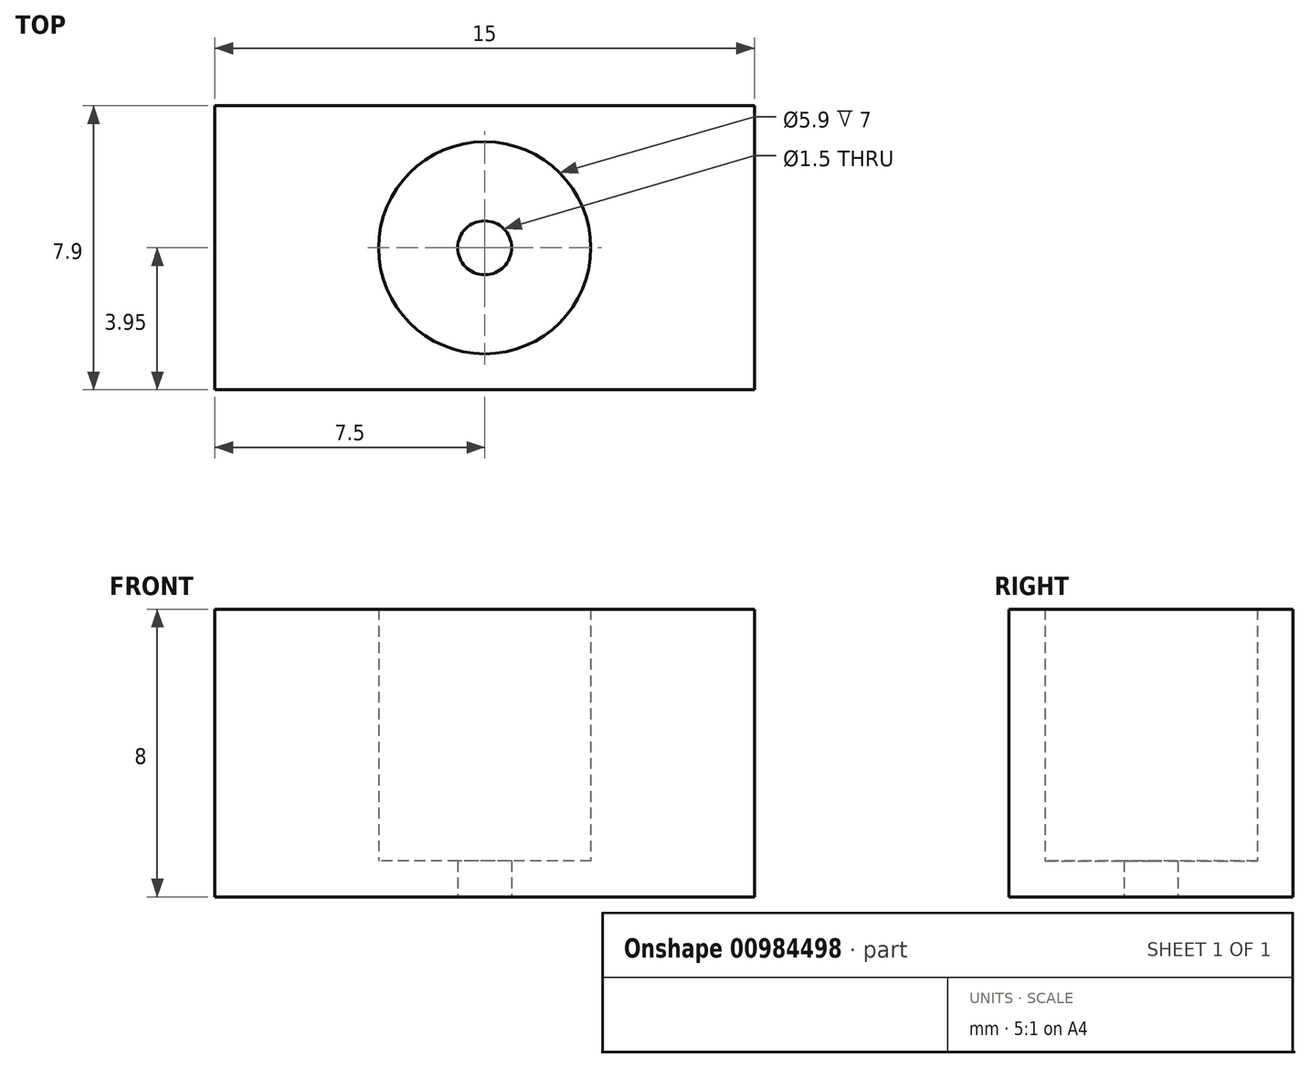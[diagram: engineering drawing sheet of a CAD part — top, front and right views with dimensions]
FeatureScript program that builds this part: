
annotation { "Feature Type Name" : "Feature", "Feature Type Description" : "" }
export const myFeature = defineFeature(function(context is Context, id is Id, definition is map)
    precondition{}
    {
        {
            var Q0;
            Q0=qCreatedBy(makeId("Top.planeOp"),FACE);
            var sketch = newSketch(context, id + "F0", { "sketchPlane" : qUnion([Q0])});
            skLineSegment(sketch, "E0", {"start": v(0, 0) * mm, "end": v(15, 0) * mm});
            skLineSegment(sketch, "E1", {"start": v(15, 0) * mm, "end": v(15, 7.9) * mm});
            skLineSegment(sketch, "E2", {"start": v(15, 7.9) * mm, "end": v(0, 7.9) * mm});
            skLineSegment(sketch, "E3", {"start": v(0, 7.9) * mm, "end": v(0, 0) * mm});
            skLineSegment(sketch, "E4", {"start": v(0, 3.95) * mm, "end": v(15, 3.95) * mm, "construction": true});
            skLineSegment(sketch, "E5", {"start": v(7.5, 0) * mm, "end": v(7.5, 7.9) * mm, "construction": true});
            skCircle(sketch, "E6", {"center": v(7.5, 3.95) * mm, "radius": 2.95 * mm});
            skCircle(sketch, "E7", {"center": v(7.5, 3.95) * mm, "radius": 0.75 * mm});
            skSolve(sketch);
        }
        {
            var Q0;
            Q0=makeQuery(id+"F0.imprint","IMPRINT",FACE,{"disambiguationData":[TD([[makeQuery(id+"F0.imprint","IMPRINT",EDGE,{"derivedFrom":sQuery(id+"F0.wireOp",EDGE,"E0")}),1.0]])]});
            extrude(context, id + "F1", {"entities" : qUnion([Q0]), "depth" : 8 * mm, "offsetDistance" : 25 * mm});
        }
        {
            var Q0;
            Q0=makeQuery(id+"F0.imprint","IMPRINT",FACE,{"disambiguationData":[TD([[makeQuery(id+"F0.imprint","IMPRINT",EDGE,{"derivedFrom":sQuery(id+"F0.wireOp",EDGE,"E6")}),1.0]])]});
            extrude(context, id + "F2", {"entities" : qUnion([Q0]), "operationType" : NewBodyOperationType.ADD, "depth" : 1 * mm, "offsetDistance" : 25 * mm});
        }
    });
